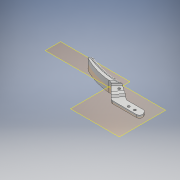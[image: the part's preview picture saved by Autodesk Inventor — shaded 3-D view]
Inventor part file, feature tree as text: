
AUTODESK INVENTOR PART (.ipt)
format: ipt  version: 2018 (Build 220112000, 112)  size: 562,688 bytes
history: native  units: mm
features: extrude x16, sketch x16, projected_geometry x6, fillet x4, chamfer x4, other x3, pattern_circular x1, mirror x1
ambient origin geometry x8: Origin, YZ Plane, XZ Plane, XY Plane, X Axis, Y Axis, Z Axis, Center Point
bodies: Body1 (feature_tree), Body2 (feature_tree), Body3 (feature_tree)
feature tree (51):
  other  "ソリッド1"
  extrude  "押し出し1"  Depth=40.0mm
  extrude  "押し出し3"  Depth=10.0mm TaperAngle=0.0deg
  extrude  "押し出し4"  Depth=7.0mm TaperAngle=0.0deg
  pattern_circular  "円形状パターン1"  [2 undecoded]
  extrude  "押し出し5"  Depth=3.0mm
  extrude  "押し出し6"  Depth=3.5mm TaperAngle=0.0deg
  extrude  "押し出し7"  Depth=40.0mm TaperAngle=360.0deg
  fillet  "フィレット1"  Radius=17.0mm
  other  "作業平面3"
  extrude  "押し出し8"  Depth=7.0mm TaperAngle=0.0deg
  chamfer  "面取り1"  Distance=15.0mm
  fillet  "フィレット2"  Radius=8.0mm
  extrude  "押し出し10"  Depth=3.0mm TaperAngle=0.0deg
  other  "作業平面2"
  mirror  "ミラー2"
  chamfer  "面取り6"  Distance=1.5mm
  chamfer  "面取り7"  Angle=45.0deg  [1 undecoded]
  fillet  "フィレット5"  Radius=30.0mm
  extrude  "押し出し11"  Depth=10.0mm
  extrude  "押し出し13"  Depth=3.0mm
  extrude  "押し出し14"  Depth=100.0mm
  extrude  "押し出し15"  Depth=24.43461mm
  extrude  "押し出し16"  Depth=30.0mm
  fillet  "フィレット6"  Radius=5.5mm
  extrude  "押し出し17"  Depth=2.0mm TaperAngle=45.0deg
  extrude  "押し出し18"  Depth=2.0mm
  extrude  "押し出し19"  Depth=4.0mm
  chamfer  "面取り8"  Distance=1.0mm
  sketch  "スケッチ1"
  sketch  "スケッチ3"
  sketch  "スケッチ4"
  sketch  "スケッチ5"
  sketch  "スケッチ7"
  sketch  "スケッチ8"
  projected_geometry  "投影ループ2"
  sketch  "スケッチ9"
  projected_geometry  "投影ループ3"
  sketch  "スケッチ10"
  sketch  "スケッチ11"
  sketch  "スケッチ12"
  projected_geometry  "投影ループ4"
  projected_geometry  "投影ループ5"
  sketch  "スケッチ13"
  sketch  "スケッチ14"
  sketch  "スケッチ15"
  sketch  "スケッチ16"
  sketch  "スケッチ17"
  projected_geometry  "投影ループ6"
  projected_geometry  "投影ループ7"
  sketch  "スケッチ18"
note: 3 required parameter values undecoded (feature->parameter linkage not recoverable at this tier; creation-order binding heuristic only, values carry confidence <= 0.55)
